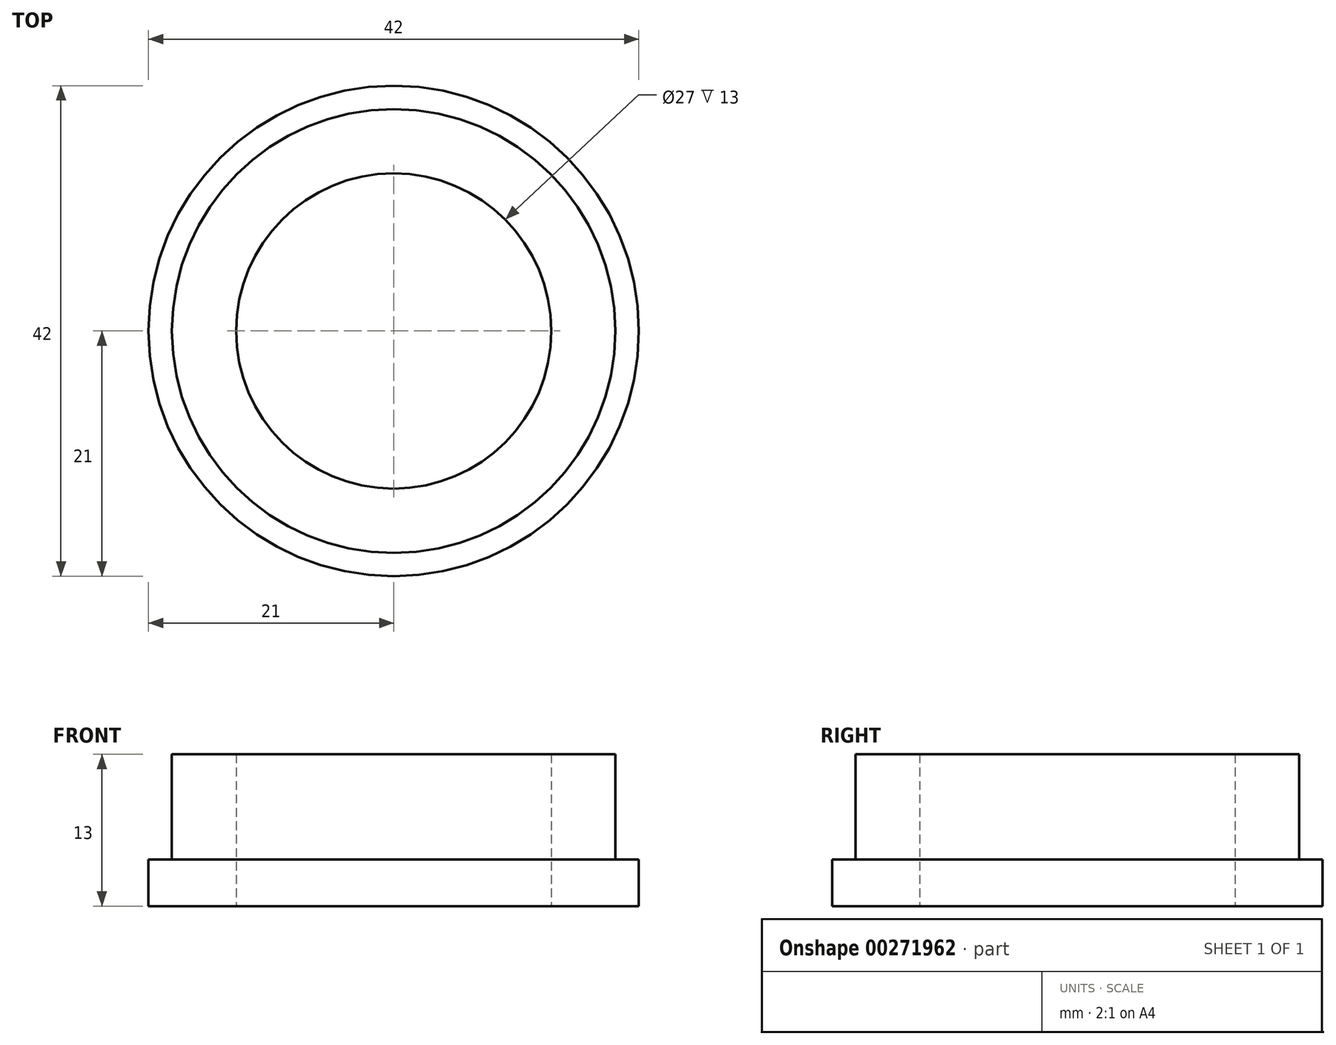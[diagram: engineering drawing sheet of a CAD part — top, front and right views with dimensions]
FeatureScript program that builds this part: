
annotation { "Feature Type Name" : "Feature", "Feature Type Description" : "" }
export const myFeature = defineFeature(function(context is Context, id is Id, definition is map)
    precondition{}
    {
        {
            var Q0;
            Q0=qCreatedBy(makeId("Front.planeOp"),FACE);
            var sketch = newSketch(context, id + "F0", { "sketchPlane" : qUnion([Q0])});
            skLineSegment(sketch, "E0", {"start": v(13.5, 0) * mm, "end": v(13.5, 13) * mm});
            skLineSegment(sketch, "E1", {"start": v(13.5, 13) * mm, "end": v(19, 13) * mm});
            skLineSegment(sketch, "E2", {"start": v(19, 13) * mm, "end": v(19, 4) * mm});
            skLineSegment(sketch, "E3", {"start": v(19, 4) * mm, "end": v(21, 4) * mm});
            skLineSegment(sketch, "E4", {"start": v(21, 4) * mm, "end": v(21, 0) * mm});
            skLineSegment(sketch, "E5", {"start": v(0, 0) * mm, "end": v(0, 25.18) * mm, "construction": true});
            skLineSegment(sketch, "E6", {"start": v(13.5, 0) * mm, "end": v(21, 0) * mm});
            skSolve(sketch);
        }
        {
            var Q0;
            Q0 = qSketchRegion(id + "F0", true);
            var Q1;
            Q1=sQuery(id+"F0.wireOp",EDGE,"E5");
            revolve(context, id + "F1", {"entities" : qUnion([Q0]), "axis" : qUnion([Q1]), "revolveType" : RevolveType.FULL});
        }
    });
